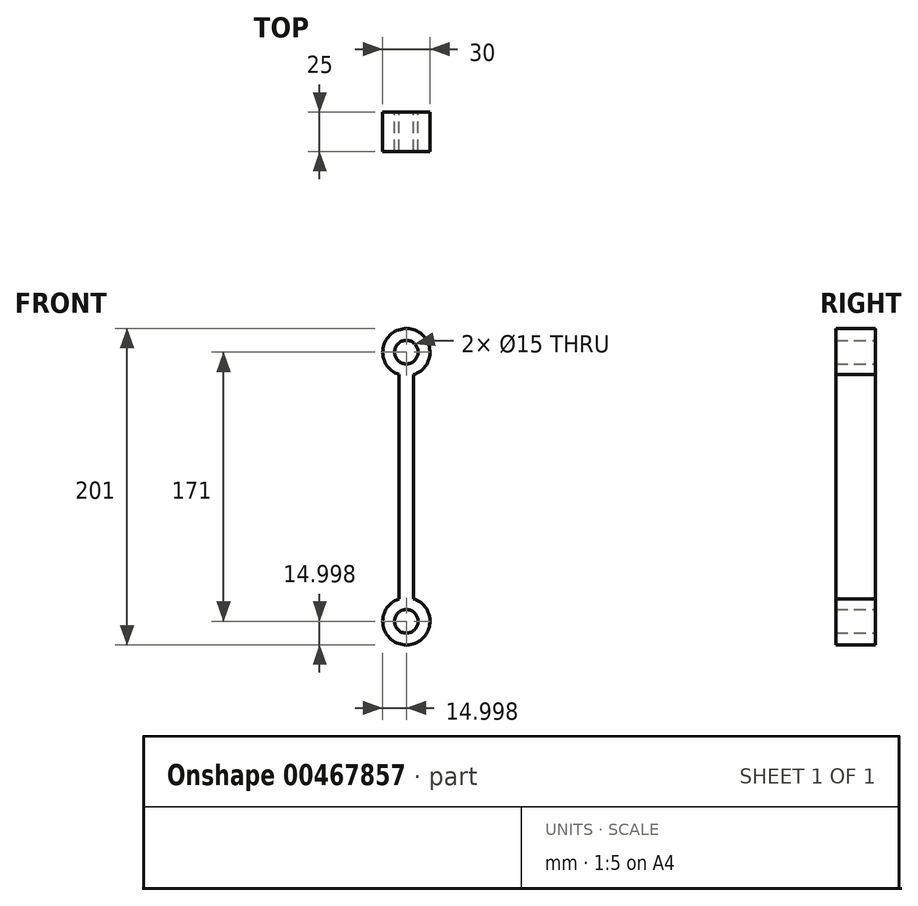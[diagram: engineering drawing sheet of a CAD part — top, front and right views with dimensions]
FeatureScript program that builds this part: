
annotation { "Feature Type Name" : "Feature", "Feature Type Description" : "" }
export const myFeature = defineFeature(function(context is Context, id is Id, definition is map)
    precondition{}
    {
        {
            var Q0;
            Q0=qCreatedBy(makeId("Front.planeOp"),FACE);
            var sketch = newSketch(context, id + "F0", { "sketchPlane" : qUnion([Q0])});
            skCircle(sketch, "E0", {"center": v(5.55, 54.18) * mm, "radius": 15 * mm});
            skCircle(sketch, "E1", {"center": v(5.55, 54.18) * mm, "radius": 7.5 * mm});
            skCircle(sketch, "E2", {"center": v(5.55, -116.82) * mm, "radius": 15 * mm});
            skCircle(sketch, "E3", {"center": v(5.55, -116.82) * mm, "radius": 7.5 * mm});
            skLineSegment(sketch, "E4", {"start": v(0.8, 39.95) * mm, "end": v(0.8, -102.6) * mm});
            skLineSegment(sketch, "E5", {"start": v(9.93, 39.83) * mm, "end": v(9.93, -102.48) * mm});
            skSolve(sketch);
        }
        {
            var Q0;
            Q0 = qSketchRegion(id + "F0", true);
            extrude(context, id + "F1", {"entities" : qUnion([Q0]), "depth" : 25 * mm});
        }
    });
